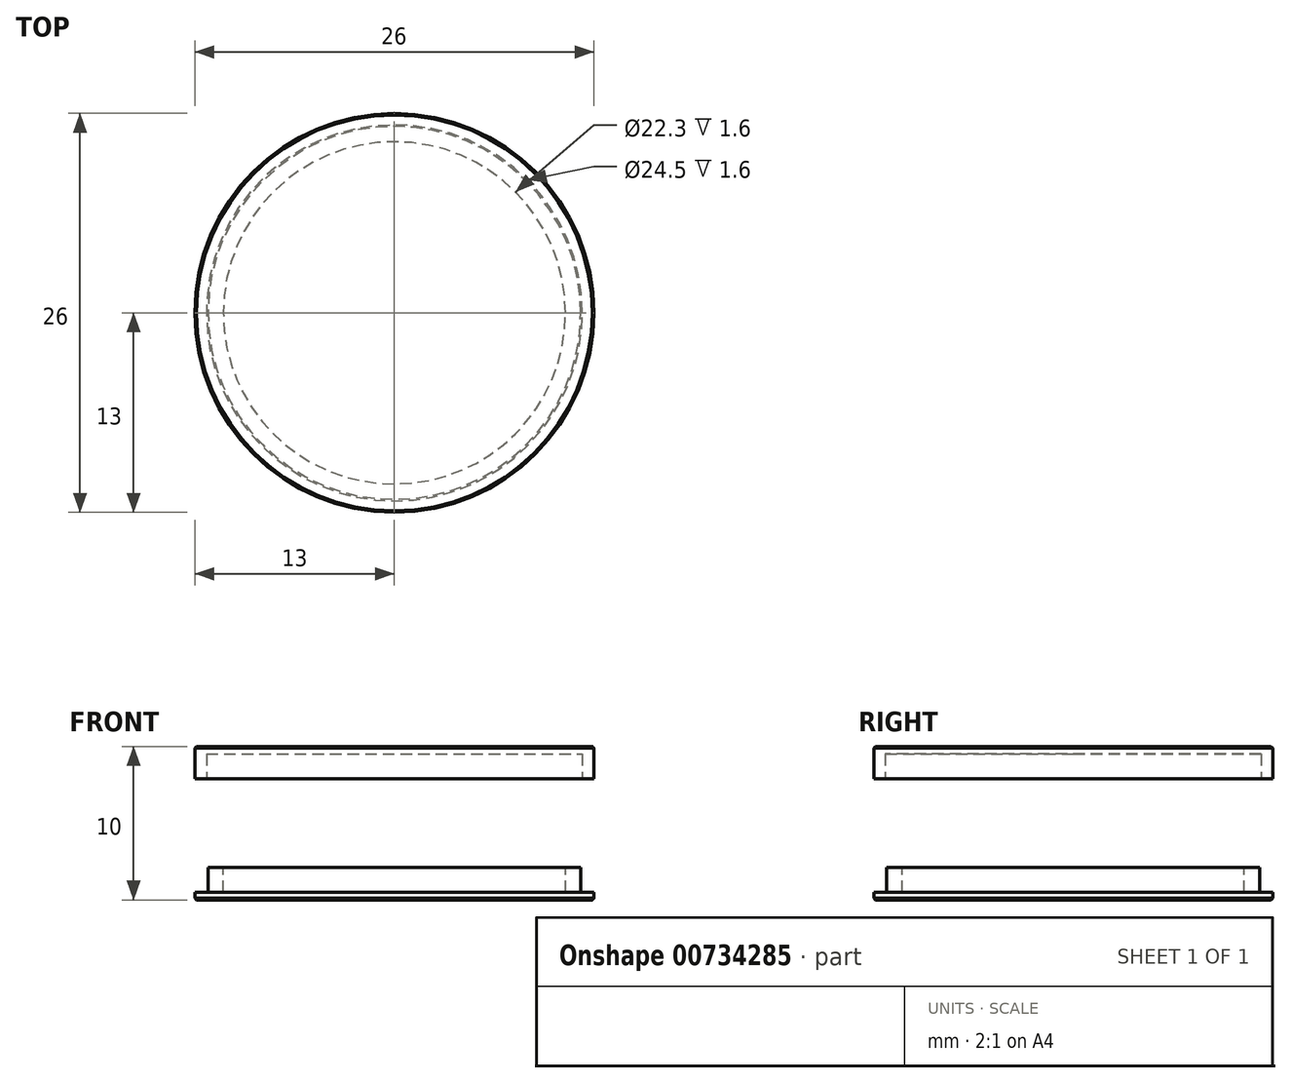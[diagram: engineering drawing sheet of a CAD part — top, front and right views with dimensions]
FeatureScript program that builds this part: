
annotation { "Feature Type Name" : "Feature", "Feature Type Description" : "" }
export const myFeature = defineFeature(function(context is Context, id is Id, definition is map)
    precondition{}
    {
        {
            var Q0;
            Q0=qCreatedBy(makeId("Top.planeOp"),FACE);
            var sketch = newSketch(context, id + "F0", { "sketchPlane" : qUnion([Q0])});
            skCircle(sketch, "E0", {"center": v(0, 0) * mm, "radius": 13 * mm});
            skSolve(sketch);
        }
        {
            var Q0;
            Q0=makeQuery(id+"F0.imprint","IMPRINT",FACE,{"disambiguationData":[TD([[makeQuery(id+"F0.imprint","IMPRINT",EDGE,{"derivedFrom":sQuery(id+"F0.wireOp",EDGE,"E0")}),1.0]])]});
            extrude(context, id + "F1", {"entities" : qUnion([Q0]), "depth" : 0.5 * mm, "offsetDistance" : 25 * mm});
        }
        {
            var Q0;
            Q0=makeQuery(id+"F1.opExtrude","CAP_FACE",FACE,{"disambiguationData":[OSD([sQuery(id+"F0.wireOp",EDGE,"E0")])],"isStart":false});
            var sketch = newSketch(context, id + "F2", { "sketchPlane" : qUnion([Q0])});
            skCircle(sketch, "E1", {"center": v(0, 0) * mm, "radius": 12.15 * mm});
            skSolve(sketch);
        }
        {
            var Q0;
            Q0=makeQuery(id+"F2.imprint","IMPRINT",FACE,{"disambiguationData":[TD([[makeQuery(id+"F2.imprint","IMPRINT",EDGE,{"derivedFrom":sQuery(id+"F2.wireOp",EDGE,"E1")}),1.0]])]});
            extrude(context, id + "F3", {"entities" : qUnion([Q0]), "operationType" : NewBodyOperationType.ADD, "depth" : 1.6 * mm, "offsetDistance" : 25 * mm});
        }
        {
            var Q0;
            Q0=makeQuery(id+"F3.opExtrude","CAP_FACE",FACE,{"disambiguationData":[OSD([sQuery(id+"F2.wireOp",EDGE,"E1")])],"isStart":false});
            var sketch = newSketch(context, id + "F4", { "sketchPlane" : qUnion([Q0])});
            skCircle(sketch, "E2", {"center": v(0, 0) * mm, "radius": 11.15 * mm});
            skSolve(sketch);
        }
        {
            var Q0;
            Q0=makeQuery(id+"F4.imprint","IMPRINT",FACE,{"disambiguationData":[TD([[makeQuery(id+"F4.imprint","IMPRINT",EDGE,{"derivedFrom":sQuery(id+"F4.wireOp",EDGE,"E2")}),1.0]])]});
            extrude(context, id + "F5", {"entities" : qUnion([Q0]), "operationType" : NewBodyOperationType.REMOVE, "oppositeDirection" : true, "depth" : 1.6 * mm, "offsetDistance" : 25 * mm});
        }
        {
            var Q0;
            Q0=qCreatedBy(makeId("Top.planeOp"),FACE);
            cPlane(context, id + "F6", {"entities" : qUnion([Q0]), "cplaneType" : CPlaneType.OFFSET, "offset" : 10 * mm, "width" : 150 * mm, "height" : 150 * mm});
        }
        {
            var Q0;
            Q0=qCreatedBy(id+"F6.planeOp",FACE);
            var sketch = newSketch(context, id + "F7", { "sketchPlane" : qUnion([Q0])});
            skCircle(sketch, "E3", {"center": v(0, 0) * mm, "radius": 13 * mm});
            skSolve(sketch);
        }
        {
            var Q0;
            Q0=makeQuery(id+"F7.imprint","IMPRINT",FACE,{"disambiguationData":[TD([[makeQuery(id+"F7.imprint","IMPRINT",EDGE,{"derivedFrom":sQuery(id+"F7.wireOp",EDGE,"E3")}),1.0]])]});
            extrude(context, id + "F8", {"entities" : qUnion([Q0]), "oppositeDirection" : true, "depth" : (2.8 - 0.7) * mm, "offsetDistance" : 25 * mm});
        }
        {
            var Q0;
            Q0=makeQuery(id+"F8.opExtrude","CAP_FACE",FACE,{"disambiguationData":[OSD([sQuery(id+"F7.wireOp",EDGE,"E3")])],"isStart":false});
            var sketch = newSketch(context, id + "F9", { "sketchPlane" : qUnion([Q0])});
            skCircle(sketch, "E4", {"center": v(0, 0) * mm, "radius": 12.25 * mm});
            skSolve(sketch);
        }
        {
            var Q0;
            Q0=makeQuery(id+"F9.imprint","IMPRINT",FACE,{"disambiguationData":[TD([[makeQuery(id+"F9.imprint","IMPRINT",EDGE,{"derivedFrom":sQuery(id+"F9.wireOp",EDGE,"E4")}),1.0]])]});
            extrude(context, id + "F10", {"entities" : qUnion([Q0]), "operationType" : NewBodyOperationType.REMOVE, "oppositeDirection" : true, "depth" : 1.6 * mm, "offsetDistance" : 25 * mm});
        }
        {
            var Q0;
            Q0=makeQuery(id+"F8.opExtrude","CAP_EDGE",EDGE,{"disambiguationData":[OSD([sQuery(id+"F7.wireOp",EDGE,"E3")])],"isStart":true});
            var Q1;
            Q1=makeQuery(id+"F1.opExtrude","CAP_EDGE",EDGE,{"disambiguationData":[OSD([sQuery(id+"F0.wireOp",EDGE,"E0")])],"isStart":true});
            chamfer(context, id + "F11", {"entities" : qUnion([Q0, Q1]), "width" : 0.1 * mm, "tangentPropagation" : true});
        }
    });
